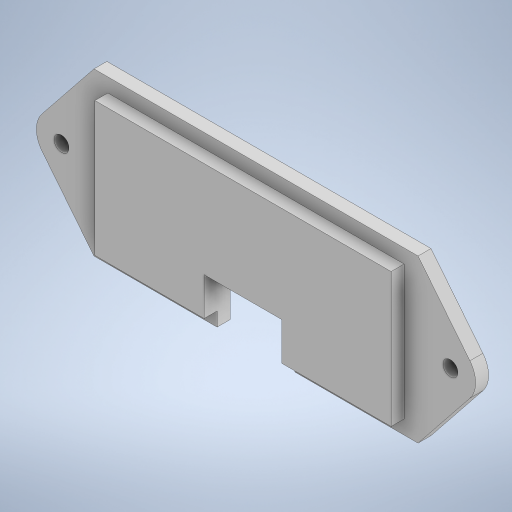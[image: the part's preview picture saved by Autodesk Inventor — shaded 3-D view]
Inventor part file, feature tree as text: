
AUTODESK INVENTOR PART (.ipt)
format: ipt  version: 2024 (Build 280153000, 153)  size: 259,584 bytes
history: native  units: mm
features: extrude x3, sketch x3, fillet x1
ambient origin geometry x8: Origin, YZ Plane, XZ Plane, XY Plane, X Axis, Y Axis, Z Axis, Center Point
bodies: Solid1 (feature_tree)
feature tree (7):
  extrude  "Extrusion1"  Depth=25.0mm
  extrude  "Extrusion4"  Depth=2.0mm
  extrude  "Extrusion5"  Depth=10.0mm
  fillet  "Fillet1"  Radius=2.3mm
  sketch  "Sketch1"  dims[d0=50.0mm d1=25.0mm]
  sketch  "Sketch4"  dims[d2=2.0mm d3=0.0mm d18=12.5mm]
  sketch  "Sketch5"  dims[d19=10.0mm d20=10.0mm d21=2.3mm d22=2.3mm d23=5.0mm d24=5.0mm d25=20.7mm d26=2.15mm d27=45.7mm d28=2.15mm d29=2.0mm d30=0.0mm d31=19.0mm d32=12.0mm d33=8.0mm d34=0.0mm d35=0.0mm d36=4.0mm]
